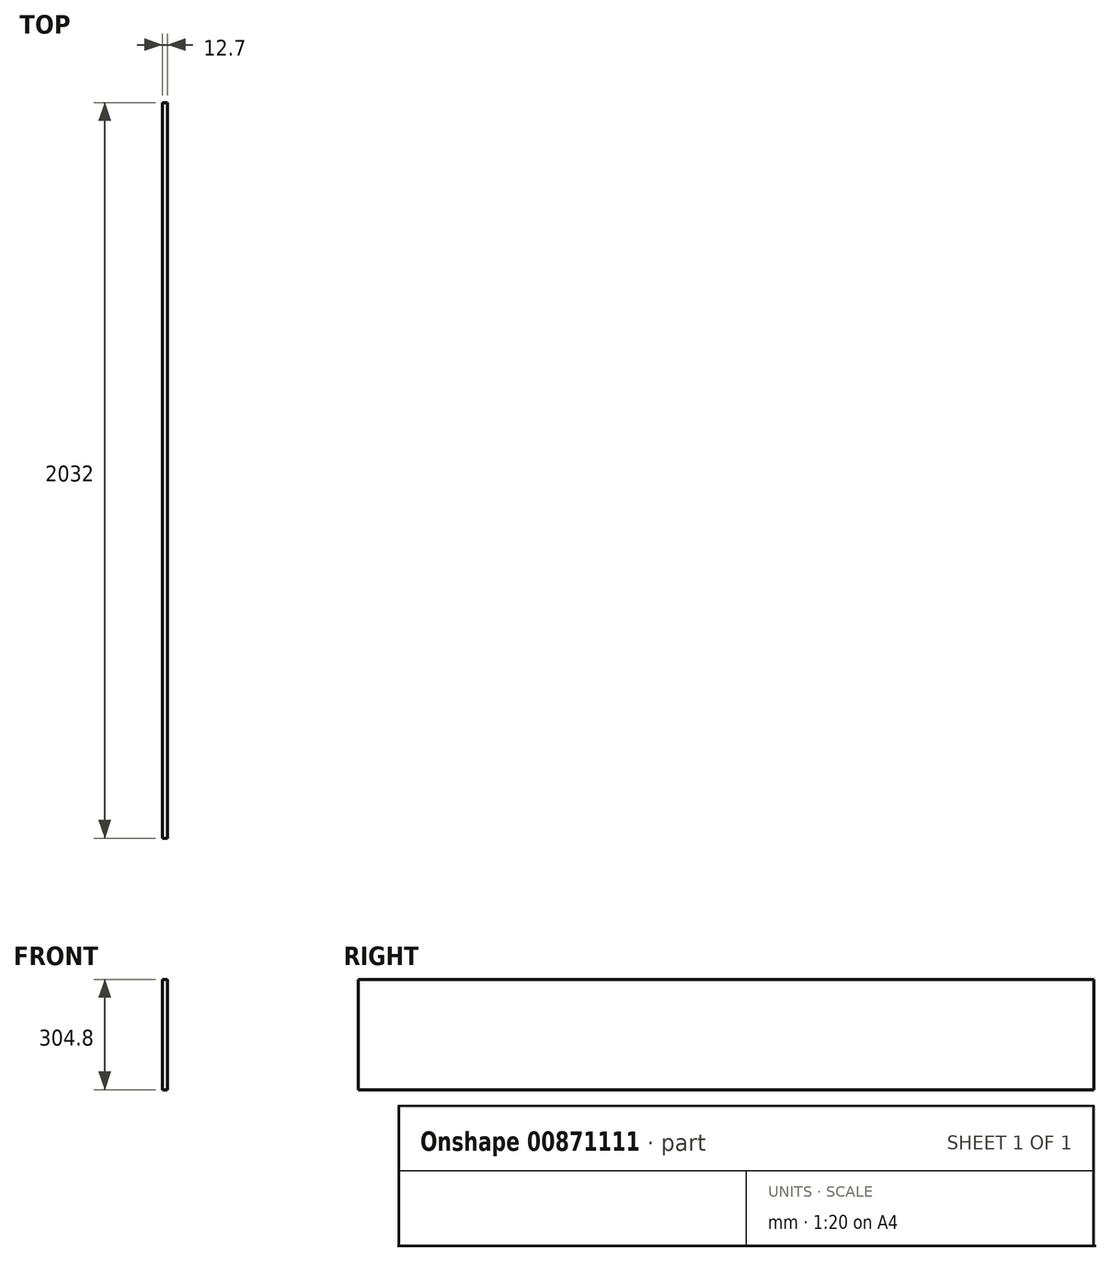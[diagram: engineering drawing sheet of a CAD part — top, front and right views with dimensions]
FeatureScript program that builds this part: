
annotation { "Feature Type Name" : "Feature", "Feature Type Description" : "" }
export const myFeature = defineFeature(function(context is Context, id is Id, definition is map)
    precondition{}
    {
        {
            var Q0;
            Q0=qCreatedBy(makeId("Right.planeOp"),FACE);
            var sketch = newSketch(context, id + "F0", { "sketchPlane" : qUnion([Q0])});
            skLineSegment(sketch, "E0.bottom", {"start": v(-1016, 152.4) * mm, "end": v(1016, 152.4) * mm});
            skLineSegment(sketch, "E0.top", {"start": v(-1016, -152.4) * mm, "end": v(1016, -152.4) * mm});
            skLineSegment(sketch, "E0.left", {"start": v(-1016, 152.4) * mm, "end": v(-1016, -152.4) * mm});
            skLineSegment(sketch, "E0.right", {"start": v(1016, 152.4) * mm, "end": v(1016, -152.4) * mm});
            skPoint(sketch, "E0.middle", {"position": v(0, 0) * mm});
            skSolve(sketch);
        }
        {
            var Q0;
            Q0 = qSketchRegion(id + "F0", true);
            extrude(context, id + "F1", {"entities" : qUnion([Q0]), "endBound" : BoundingType.SYMMETRIC, "depth" : 12.7 * mm, "offsetDistance" : 25.4 * mm});
        }
    });
